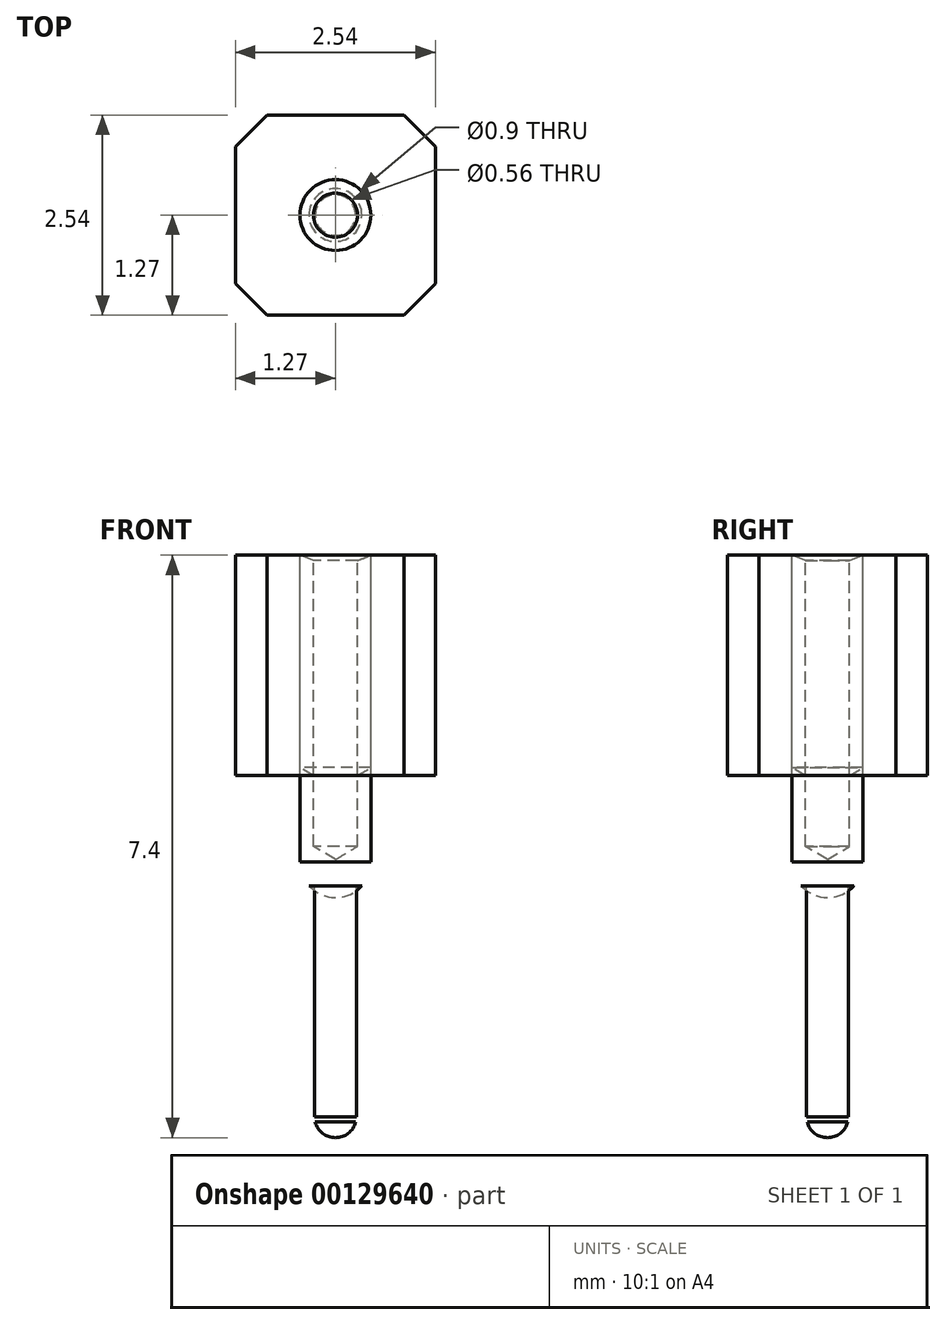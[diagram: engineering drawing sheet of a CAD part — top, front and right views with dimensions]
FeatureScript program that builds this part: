
annotation { "Feature Type Name" : "Feature", "Feature Type Description" : "" }
export const myFeature = defineFeature(function(context is Context, id is Id, definition is map)
    precondition{}
    {
        {
            var Q0;
            Q0=qCreatedBy(makeId("Top.planeOp"),FACE);
            var sketch = newSketch(context, id + "F0", { "sketchPlane" : qUnion([Q0])});
            skLineSegment(sketch, "E0", {"start": v(0, 0) * mm, "end": v(-1.27, 0) * mm});
            skCircle(sketch, "E1", {"center": v(-1.27, 0) * mm, "radius": 0.27 * mm});
            skCircle(sketch, "E2", {"center": v(-1.27, 0) * mm, "radius": 0.45 * mm});
            skCircle(sketch, "E3", {"center": v(-1.27, 0) * mm, "radius": 0.28 * mm});
            skSolve(sketch);
        }
        {
            var Q0;
            Q0=makeQuery(id+"F0.imprint","IMPRINT",FACE,{"disambiguationData":[TD([[makeQuery(id+"F0.imprint","IMPRINT",EDGE,{"derivedFrom":sQuery(id+"F0.wireOp",EDGE,"E1")}),1.0]])]});
            extrude(context, id + "F1", {"entities" : qUnion([Q0]), "oppositeDirection" : true, "depth" : 7.4 * mm, "hasSecondDirection" : true, "secondDirectionOppositeDirection" : true, "secondDirectionDepth" : 4.2 * mm});
        }
        {
            var Q0;
            Q0=qCreatedBy(makeId("Top.planeOp"),FACE);
            var sketch = newSketch(context, id + "F2", { "sketchPlane" : qUnion([Q0])});
            skLineSegment(sketch, "E4", {"start": v(0, 0) * mm, "end": v(-1.27, 0) * mm});
            skPoint(sketch, "E5.middle", {"position": v(-1.27, 0) * mm});
            skCircle(sketch, "E6", {"center": v(-1.27, 0) * mm, "radius": 0.45 * mm});
            skSolve(sketch);
        }
        {
            var Q0;
            Q0=makeQuery(id+"F2.imprint","IMPRINT",FACE,{"disambiguationData":[TD([[makeQuery(id+"F2.imprint","IMPRINT",EDGE,{"derivedFrom":sQuery(id+"F2.wireOp",EDGE,"E6")}),1.0]])]});
            extrude(context, id + "F3", {"entities" : qUnion([Q0]), "oppositeDirection" : true, "depth" : 4.2 * mm});
        }
        {
            var Q0;
            Q0=qCreatedBy(makeId("Top.planeOp"),FACE);
            var sketch = newSketch(context, id + "F4", { "sketchPlane" : qUnion([Q0])});
            skLineSegment(sketch, "E7", {"start": v(0, 0) * mm, "end": v(-1.27, 0) * mm});
            skLineSegment(sketch, "E8.bottom", {"start": v(-2.54, 1.27) * mm, "end": v(0, 1.27) * mm});
            skLineSegment(sketch, "E8.top", {"start": v(-2.54, -1.27) * mm, "end": v(0, -1.27) * mm});
            skLineSegment(sketch, "E8.left", {"start": v(-2.54, 1.27) * mm, "end": v(-2.54, -1.27) * mm});
            skLineSegment(sketch, "E8.right", {"start": v(0, 1.27) * mm, "end": v(0, -1.27) * mm});
            skPoint(sketch, "E8.middle", {"position": v(-1.27, 0) * mm});
            skSolve(sketch);
        }
        {
            var Q0;
            {var subQ2=sQuery(id+"F4.wireOp",EDGE,"E8.bottom");Q0=makeQuery(id+"F4.imprint","IMPRINT",FACE,{"disambiguationData":[TD([[makeQuery(id+"F4.imprint","IMPRINT",EDGE,{"derivedFrom":subQ2}),-1.0]])]});}
            extrude(context, id + "F5", {"entities" : qUnion([Q0]), "oppositeDirection" : true, "depth" : 2.8 * mm});
        }
        {
            var Q0;
            Q0=qCreatedBy(makeId("Top.planeOp"),FACE);
            var sketch = newSketch(context, id + "F6", { "sketchPlane" : qUnion([Q0])});
            skLineSegment(sketch, "E9", {"start": v(0, 0) * mm, "end": v(-1.27, 0) * mm});
            skCircle(sketch, "E10", {"center": v(-1.27, 0) * mm, "radius": 0.28 * mm});
            skSolve(sketch);
        }
        {
            var Q0;
            Q0=sQuery(id+"F6.wireOp",VERTEX,"E10.center");
            var Q1;
            Q1=makeQuery(id+"F3.opExtrude","SWEPT_BODY",BODY,{"disambiguationData":[OSD([sQuery(id+"F2.wireOp",EDGE,"E6")])]});
            var Q2;
            Q2=makeQuery(id+"F5.opExtrude","SWEPT_BODY",BODY,{"disambiguationData":[OSD([sQuery(id+"F4.wireOp",EDGE,"E8.bottom"),sQuery(id+"F4.wireOp",EDGE,"E8.top"),sQuery(id+"F4.wireOp",EDGE,"E8.left"),sQuery(id+"F4.wireOp",EDGE,"E8.right")])]});
            hole(context, id + "F7", {"style" : HoleStyle.C_SINK, "endStyle" : HoleEndStyle.BLIND, "holeDiameter" : 0.56 * mm, "cSinkDiameter" : 0.9 * mm, "cSinkAngle" : 135 * degree, "holeDepth" : 3.7 * mm, "locations" : qUnion([Q0]), "scope" : qUnion([Q1, Q2])});
        }
        {
            var Q0;
            Q0=makeQuery(id+"F1.opExtrude","CAP_FACE",FACE,{"disambiguationData":[OSD([sQuery(id+"F0.wireOp",EDGE,"E1")])],"isStart":false});
            extrude(context, id + "F8", {"entities" : qUnion([Q0]), "operationType" : NewBodyOperationType.REMOVE, "oppositeDirection" : true, "depth" : 0.2 * mm});
        }
        {
            var Q0;
            Q0=makeQuery(id+"F5.opExtrude","SWEPT_EDGE",EDGE,{"disambiguationData":[OSD([sQuery(id+"F4.wireOp",EDGE,"E8.top"),sQuery(id+"F4.wireOp",EDGE,"E8.left")])]});
            var Q1;
            Q1=makeQuery(id+"F5.opExtrude","SWEPT_EDGE",EDGE,{"disambiguationData":[OSD([sQuery(id+"F4.wireOp",EDGE,"E8.top"),sQuery(id+"F4.wireOp",EDGE,"E8.right")])]});
            var Q2;
            Q2=makeQuery(id+"F5.opExtrude","SWEPT_EDGE",EDGE,{"disambiguationData":[OSD([sQuery(id+"F4.wireOp",EDGE,"E8.bottom"),sQuery(id+"F4.wireOp",EDGE,"E8.right")])]});
            var Q3;
            Q3=makeQuery(id+"F5.opExtrude","SWEPT_EDGE",EDGE,{"disambiguationData":[OSD([sQuery(id+"F4.wireOp",EDGE,"E8.bottom"),sQuery(id+"F4.wireOp",EDGE,"E8.left")])]});
            chamfer(context, id + "F9", {"entities" : qUnion([Q0, Q1, Q2, Q3]), "width" : 0.4 * mm, "tangentPropagation" : true});
        }
        {
            var Q0;
            Q0=qCreatedBy(makeId("Top.planeOp"),FACE);
            var sketch = newSketch(context, id + "F10", { "sketchPlane" : qUnion([Q0])});
            skLineSegment(sketch, "E11", {"start": v(0, 0) * mm, "end": v(1.27, 0) * mm});
            skCircle(sketch, "E12", {"center": v(1.27, 0) * mm, "radius": 0.45 * mm});
            skLineSegment(sketch, "E13", {"start": v(1.27, 0) * mm, "end": v(1.72, 0) * mm});
            skSolve(sketch);
        }
        {
            var Q0;
            {var subQ0=sQuery(id+"F10.wireOp",EDGE,"E13");Q0=makeQuery(id+"F10.imprint","IMPRINT",FACE,{"disambiguationData":[TD([[makeQuery(id+"F10.imprint","IMPRINT",EDGE,{"derivedFrom":subQ0}),1.0]])]});}
            var Q1;
            Q1=sQuery(id+"F10.wireOp",EDGE,"E11");
            revolve(context, id + "F11", {"entities" : qUnion([Q0]), "axis" : qUnion([Q1]), "revolveType" : RevolveType.ONE_DIRECTION, "oppositeDirection" : true, "angle" : 180 * degree});
        }
        {
            var Q0;
            Q0=makeQuery(id+"F11.opRevolve","SWEPT_BODY",BODY,{"disambiguationData":[OSD([sQuery(id+"F10.wireOp",EDGE,"E11"),sQuery(id+"F10.wireOp",EDGE,"E12"),sQuery(id+"F10.wireOp",EDGE,"E13")])]});
            var Q1;
            Q1=qCreatedBy(makeId("Right.planeOp"),FACE);
            transform(context, id + "F12", {"entities" : qUnion([Q0]), "transformType" : TransformType.TRANSLATION_3D, "dx" : -2.54 * mm, "dy" : 0 * mm, "dz" : -3.9 * mm, "makeCopy" : false});
        }
        {
            var Q0;
            Q0=makeQuery(id+"F3.opExtrude","CAP_FACE",FACE,{"disambiguationData":[OSD([sQuery(id+"F2.wireOp",EDGE,"E6")])],"isStart":false});
            extrude(context, id + "F13", {"entities" : qUnion([Q0]), "operationType" : NewBodyOperationType.REMOVE, "oppositeDirection" : true, "depth" : 0.3 * mm});
        }
        {
            var Q0;
            Q0=qCreatedBy(makeId("Top.planeOp"),FACE);
            var sketch = newSketch(context, id + "F14", { "sketchPlane" : qUnion([Q0])});
            skLineSegment(sketch, "E14", {"start": v(0, 0) * mm, "end": v(-1.27, 0) * mm});
            skCircle(sketch, "E15", {"center": v(-1.27, 0) * mm, "radius": 0.27 * mm});
            skLineSegment(sketch, "E16", {"start": v(-1.27, 0) * mm, "end": v(-1.54, 0) * mm});
            skSolve(sketch);
        }
        {
            var Q0;
            {var subQ0=sQuery(id+"F14.wireOp",EDGE,"E16");Q0=makeQuery(id+"F14.imprint","IMPRINT",FACE,{"disambiguationData":[TD([[makeQuery(id+"F14.imprint","IMPRINT",EDGE,{"derivedFrom":subQ0}),-1.0]])]});}
            var Q1;
            Q1=sQuery(id+"F14.wireOp",EDGE,"E16");
            revolve(context, id + "F15", {"entities" : qUnion([Q0]), "axis" : qUnion([Q1]), "revolveType" : RevolveType.ONE_DIRECTION, "angle" : 180 * degree});
        }
        {
            var Q0;
            Q0=makeQuery(id+"F15.opRevolve","SWEPT_BODY",BODY,{"disambiguationData":[OSD([sQuery(id+"F14.wireOp",EDGE,"E14"),sQuery(id+"F14.wireOp",EDGE,"E15"),sQuery(id+"F14.wireOp",EDGE,"E16")])]});
            transform(context, id + "F16", {"entities" : qUnion([Q0]), "transformType" : TransformType.TRANSLATION_3D, "dx" : 0 * mm, "dy" : 0 * mm, "dz" : -7.13 * mm, "makeCopy" : false});
        }
        {
            var Q0;
            Q0=makeQuery(id+"F8.boolean.opBoolean","COPY",FACE,{"derivedFrom":makeQuery(id+"F8.opExtrude","CAP_FACE",FACE,{"disambiguationData":[OSD([sQuery(id+"F0.wireOp",EDGE,"E1")])],"isStart":false})});
            extrude(context, id + "F17", {"entities" : qUnion([Q0]), "operationType" : NewBodyOperationType.REMOVE, "endBound" : BoundingType.UP_TO_NEXT, "oppositeDirection" : true, "depth" : 0.07 * mm});
        }
        {
            var Q0;
            Q0=qCreatedBy(makeId("Top.planeOp"),FACE);
            var sketch = newSketch(context, id + "F18", { "sketchPlane" : qUnion([Q0])});
            skLineSegment(sketch, "E17", {"start": v(0, 0) * mm, "end": v(-1.27, 0) * mm});
            skSolve(sketch);
        }
        {
            var Q0;
            Q0=sQuery(id+"F18.wireOp",VERTEX,"E17.end");
            var Q1;
            Q1=makeQuery(id+"F5.opExtrude","SWEPT_BODY",BODY,{"disambiguationData":[OSD([sQuery(id+"F4.wireOp",EDGE,"E8.bottom"),sQuery(id+"F4.wireOp",EDGE,"E8.top"),sQuery(id+"F4.wireOp",EDGE,"E8.left"),sQuery(id+"F4.wireOp",EDGE,"E8.right")])]});
            hole(context, id + "F19", {"style" : HoleStyle.SIMPLE, "endStyle" : HoleEndStyle.BLIND, "holeDiameter" : 0.9 * mm, "holeDepth" : 2.7 * mm, "locations" : qUnion([Q0]), "scope" : qUnion([Q1])});
        }
        {
            var Q0;
            Q0=makeQuery(id+"F15.opRevolve","SWEPT_BODY",BODY,{"disambiguationData":[OSD([sQuery(id+"F14.wireOp",EDGE,"E14"),sQuery(id+"F14.wireOp",EDGE,"E15"),sQuery(id+"F14.wireOp",EDGE,"E16")])]});
            var Q1;
            Q1=makeQuery(id+"F11.opRevolve","SWEPT_BODY",BODY,{"disambiguationData":[OSD([sQuery(id+"F10.wireOp",EDGE,"E11"),sQuery(id+"F10.wireOp",EDGE,"E12"),sQuery(id+"F10.wireOp",EDGE,"E13")])]});
            var Q2;
            Q2=makeQuery(id+"F5.opExtrude","SWEPT_BODY",BODY,{"disambiguationData":[OSD([sQuery(id+"F4.wireOp",EDGE,"E8.bottom"),sQuery(id+"F4.wireOp",EDGE,"E8.top"),sQuery(id+"F4.wireOp",EDGE,"E8.left"),sQuery(id+"F4.wireOp",EDGE,"E8.right")])]});
            var Q3;
            Q3=makeQuery(id+"F1.opExtrude","SWEPT_BODY",BODY,{"disambiguationData":[OSD([sQuery(id+"F0.wireOp",EDGE,"E1")])]});
            var Q4;
            Q4=makeQuery(id+"F3.opExtrude","SWEPT_BODY",BODY,{"disambiguationData":[OSD([sQuery(id+"F2.wireOp",EDGE,"E6")])]});
            transform(context, id + "F20", {"entities" : qUnion([Q0, Q1, Q2, Q3, Q4]), "transformType" : TransformType.TRANSLATION_3D, "dx" : 0 * mm, "dy" : 0 * mm, "dz" : 4.2 * mm, "makeCopy" : false});
        }
    });
